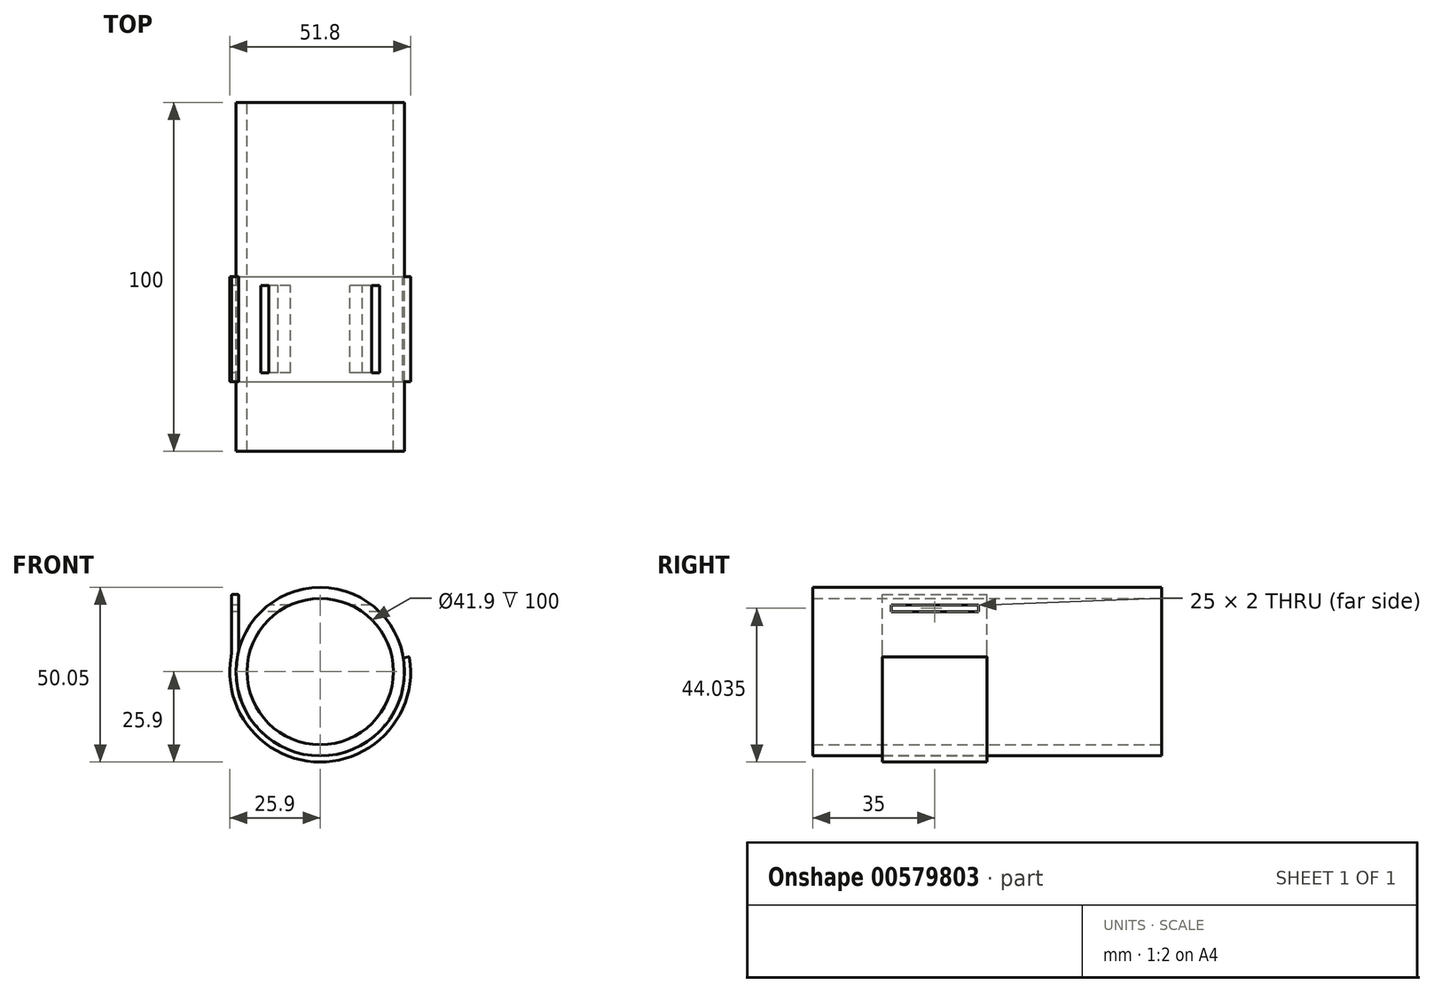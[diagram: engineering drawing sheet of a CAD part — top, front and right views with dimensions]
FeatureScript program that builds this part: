
annotation { "Feature Type Name" : "Feature", "Feature Type Description" : "" }
export const myFeature = defineFeature(function(context is Context, id is Id, definition is map)
    precondition{}
    {
        {
            var Q0;
            Q0=qCreatedBy(makeId("Front.planeOp"),FACE);
            var sketch = newSketch(context, id + "F0", { "sketchPlane" : qUnion([Q0])});
            skCircle(sketch, "E0", {"center": v(0, 0) * mm, "radius": 20.95 * mm});
            skCircle(sketch, "E1", {"center": v(0, 0) * mm, "radius": 24.15 * mm});
            skSolve(sketch);
        }
        {
            var Q0;
            Q0 = qSketchRegion(id + "F0", true);
            extrude(context, id + "F1", {"entities" : qUnion([Q0]), "endBound" : BoundingType.SYMMETRIC, "depth" : 100 * mm, "offsetDistance" : 25 * mm});
        }
        {
            var Q0;
            Q0=qCreatedBy(makeId("Front.planeOp"),FACE);
            var sketch = newSketch(context, id + "F2", { "sketchPlane" : qUnion([Q0])});
            skLineSegment(sketch, "E2", {"start": v(0, 0) * mm, "end": v(22.7, 8.26) * mm, "construction": true});
            skLineSegment(sketch, "E3", {"start": v(0, 0) * mm, "end": v(24.1, 8.77) * mm, "construction": true});
            skLineSegment(sketch, "E4", {"start": v(-25.39, 6.05) * mm, "end": v(-25.39, 21.89) * mm});
            skLineSegment(sketch, "E5", {"start": v(-23.39, 5.92) * mm, "end": v(-23.39, 21.89) * mm});
            skPoint(sketch, "E6.visualSharp", {"position": v(-25.39, 5.11) * mm});
            skArc(sketch, "E6.filletArc", {"start": v(-25.55, 4.25) * mm, "mid": v(-25.43, 5.14) * mm, "end": v(-25.39, 6.05) * mm});
            skPoint(sketch, "E7.visualSharp", {"position": v(-23.39, 5) * mm});
            skPoint(sketch, "E8.newPointB", {"position": v(0, 22.65) * mm});
            skArc(sketch, "E9.filletArc", {"start": v(-23.59, 3.93) * mm, "mid": v(-23.44, 4.92) * mm, "end": v(-23.39, 5.92) * mm});
            skArc(sketch, "E10", {"start": v(-25.55, 4.25) * mm, "mid": v(-0.13, -25.9) * mm, "end": v(25.59, 4) * mm});
            skArc(sketch, "E11", {"start": v(-23.59, 3.93) * mm, "mid": v(-0.12, -23.9) * mm, "end": v(23.63, 3.69) * mm});
            skLineSegment(sketch, "E12", {"start": v(-23.64, 22.14) * mm, "end": v(-25.14, 22.14) * mm});
            skPoint(sketch, "E13.visualSharp", {"position": v(-25.39, 22.14) * mm});
            skArc(sketch, "E13.filletArc", {"start": v(-25.14, 22.14) * mm, "mid": v(-25.31, 22.06) * mm, "end": v(-25.39, 21.89) * mm});
            skPoint(sketch, "E14.visualSharp", {"position": v(-23.39, 22.14) * mm});
            skArc(sketch, "E14.filletArc", {"start": v(-23.39, 21.89) * mm, "mid": v(-23.46, 22.06) * mm, "end": v(-23.64, 22.14) * mm});
            skLineSegment(sketch, "E15", {"start": v(25.3, 4.21) * mm, "end": v(23.83, 3.97) * mm});
            skPoint(sketch, "E16.visualSharp", {"position": v(23.59, 3.93) * mm});
            skArc(sketch, "E16.filletArc", {"start": v(23.83, 3.97) * mm, "mid": v(23.67, 3.87) * mm, "end": v(23.63, 3.69) * mm});
            skPoint(sketch, "E17.visualSharp", {"position": v(25.55, 4.25) * mm});
            skArc(sketch, "E17.filletArc", {"start": v(25.59, 4) * mm, "mid": v(25.49, 4.17) * mm, "end": v(25.3, 4.21) * mm});
            skLineSegment(sketch, "E18", {"start": v(7.62, -24.75) * mm, "end": v(2.25, 8.31) * mm, "construction": true});
            skSolve(sketch);
        }
        {
            var Q0;
            Q0=makeQuery(id+"F2.imprint","IMPRINT",FACE,{"disambiguationData":[TD([[makeQuery(id+"F2.imprint","IMPRINT",EDGE,{"derivedFrom":sQuery(id+"F2.wireOp",EDGE,"E4")}),-1.0]])]});
            extrude(context, id + "F3", {"entities" : qUnion([Q0]), "depth" : 30 * mm, "offsetDistance" : 25 * mm});
        }
        {
            var Q0;
            Q0=makeQuery(id+"F3.opExtrude","SWEPT_EDGE",EDGE,{"disambiguationData":[OSD([sQuery(id+"F2.wireOp",EDGE,"E11"),sQuery(id+"F2.wireOp",EDGE,"E15")])]});
            var Q1;
            Q1=makeQuery(id+"F3.opExtrude","SWEPT_EDGE",EDGE,{"disambiguationData":[OSD([sQuery(id+"F2.wireOp",EDGE,"E10"),sQuery(id+"F2.wireOp",EDGE,"E15")])]});
            fillet(context, id + "F4", {"entities" : qUnion([Q0, Q1]), "radius" : 0.25 * mm, "tangentPropagation" : true, "allowEdgeOverflow" : false});
        }
        {
            var Q0;
            Q0=makeQuery(id+"F3.opExtrude","SWEPT_FACE",FACE,{"disambiguationData":[OSD([sQuery(id+"F2.wireOp",EDGE,"E4")])]});
            var sketch = newSketch(context, id + "F5", { "sketchPlane" : qUnion([Q0])});
            skLineSegment(sketch, "E19.bottom", {"start": v(27.5, 17.14) * mm, "end": v(2.5, 17.14) * mm});
            skLineSegment(sketch, "E19.top", {"start": v(27.5, 19.14) * mm, "end": v(2.5, 19.14) * mm});
            skLineSegment(sketch, "E19.left", {"start": v(27.5, 17.14) * mm, "end": v(27.5, 19.14) * mm});
            skLineSegment(sketch, "E19.right", {"start": v(2.5, 17.14) * mm, "end": v(2.5, 19.14) * mm});
            skPoint(sketch, "E19.middle", {"position": v(15, 18.14) * mm});
            skSolve(sketch);
        }
        {
            var Q0;
            Q0=makeQuery(id+"F5.imprint","IMPRINT",FACE,{"disambiguationData":[TD([[makeQuery(id+"F5.imprint","IMPRINT",EDGE,{"derivedFrom":sQuery(id+"F5.wireOp",EDGE,"E19.bottom")}),-1.0]])]});
            extrude(context, id + "F6", {"entities" : qUnion([Q0]), "operationType" : NewBodyOperationType.REMOVE, "endBound" : BoundingType.THROUGH_ALL, "oppositeDirection" : true, "depth" : 25 * mm, "offsetDistance" : 25 * mm});
        }
    });
